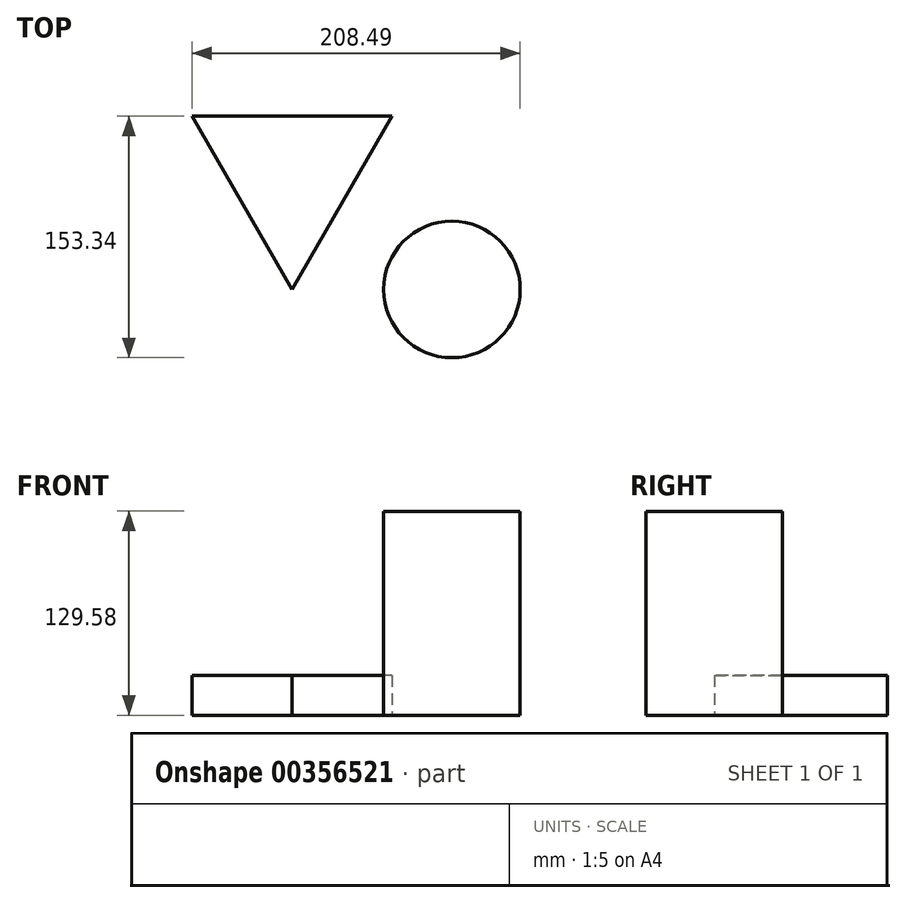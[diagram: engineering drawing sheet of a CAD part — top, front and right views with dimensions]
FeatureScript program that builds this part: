
annotation { "Feature Type Name" : "Feature", "Feature Type Description" : "" }
export const myFeature = defineFeature(function(context is Context, id is Id, definition is map)
    precondition{}
    {
        {
            var Q0;
            Q0=qCreatedBy(makeId("Top.planeOp"),FACE);
            var sketch = newSketch(context, id + "F0", { "sketchPlane" : qUnion([Q0])});
            skLineSegment(sketch, "E0", {"start": v(0, 0) * mm, "end": v(-63.5, 109.99) * mm});
            skLineSegment(sketch, "E1", {"start": v(-63.5, 109.99) * mm, "end": v(63.5, 109.99) * mm});
            skLineSegment(sketch, "E2", {"start": v(63.5, 109.99) * mm, "end": v(0, 0) * mm});
            skSolve(sketch);
        }
        {
            var Q0;
            Q0 = qSketchRegion(id + "F0", true);
            extrude(context, id + "F1", {"entities" : qUnion([Q0]), "depth" : 25.4 * mm});
        }
        {
            var Q0;
            Q0=qCreatedBy(makeId("Top.planeOp"),FACE);
            var sketch = newSketch(context, id + "F2", { "sketchPlane" : qUnion([Q0])});
            skCircle(sketch, "E3", {"center": v(101.64, 0) * mm, "radius": 43.35 * mm});
            skSolve(sketch);
        }
        {
            var Q0;
            Q0=makeQuery(id+"F2.imprint","IMPRINT",FACE,{"disambiguationData":[TD([[makeQuery(id+"F2.imprint","IMPRINT",EDGE,{"derivedFrom":sQuery(id+"F2.wireOp",EDGE,"E3")}),1.0]])]});
            extrude(context, id + "F3", {"entities" : qUnion([Q0]), "depth" : 129.58 * mm});
        }
    });
